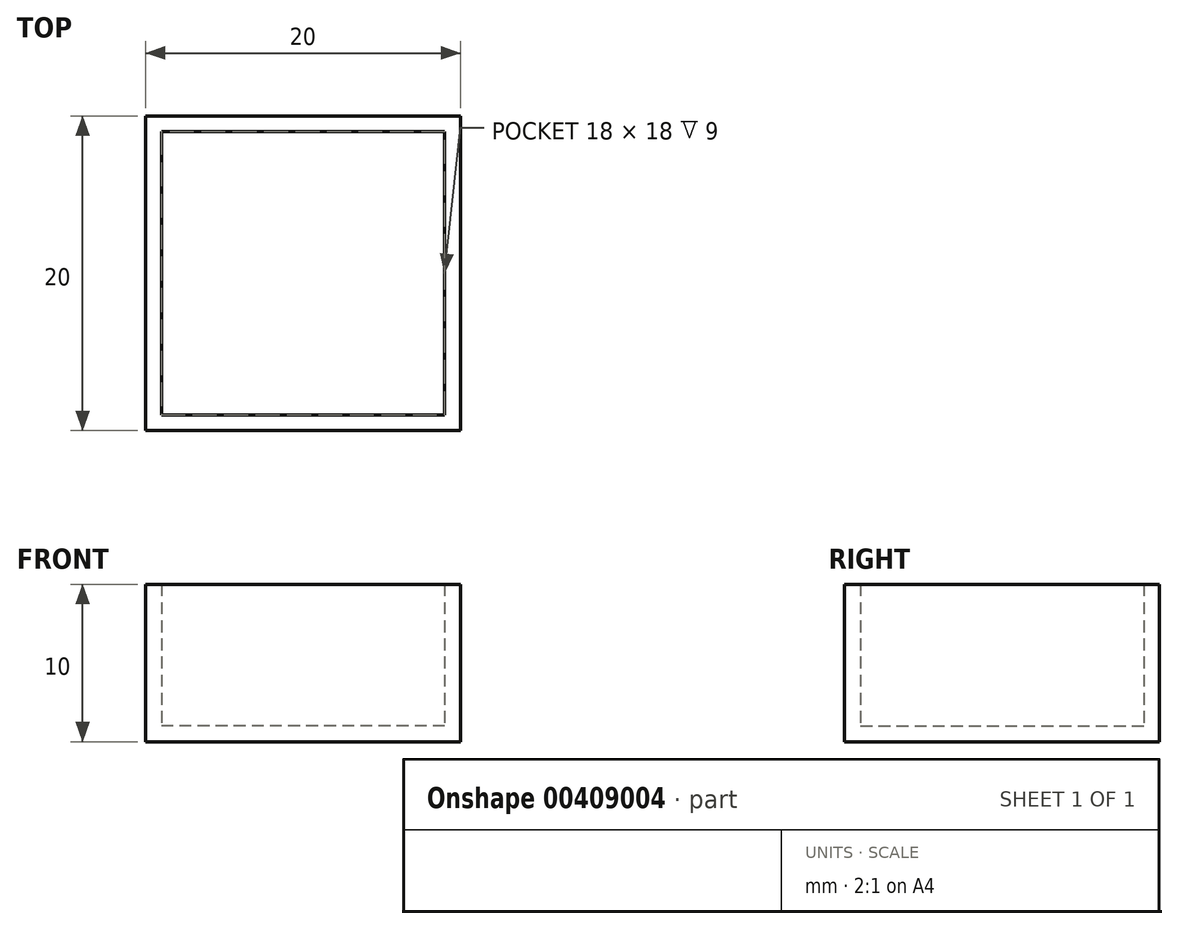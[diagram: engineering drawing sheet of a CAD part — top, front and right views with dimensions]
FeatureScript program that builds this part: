
annotation { "Feature Type Name" : "Feature", "Feature Type Description" : "" }
export const myFeature = defineFeature(function(context is Context, id is Id, definition is map)
    precondition{}
    {
        {
            var Q0;
            Q0=qCreatedBy(makeId("Top.planeOp"),FACE);
            var sketch = newSketch(context, id + "F0", { "sketchPlane" : qUnion([Q0])});
            skLineSegment(sketch, "E0.bottom", {"start": v(-10, 10) * mm, "end": v(10, 10) * mm});
            skLineSegment(sketch, "E0.top", {"start": v(-10, -10) * mm, "end": v(10, -10) * mm});
            skLineSegment(sketch, "E0.left", {"start": v(-10, 10) * mm, "end": v(-10, -10) * mm});
            skLineSegment(sketch, "E0.right", {"start": v(10, 10) * mm, "end": v(10, -10) * mm});
            skPoint(sketch, "E0.middle", {"position": v(0, 0) * mm});
            skLineSegment(sketch, "E1.0", {"start": v(-9, 9) * mm, "end": v(9, 9) * mm});
            skLineSegment(sketch, "E1.1", {"start": v(-9, 9) * mm, "end": v(-9, -9) * mm});
            skLineSegment(sketch, "E1.2", {"start": v(-9, -9) * mm, "end": v(9, -9) * mm});
            skLineSegment(sketch, "E1.3", {"start": v(9, 9) * mm, "end": v(9, -9) * mm});
            skSolve(sketch);
        }
        {
            var Q0;
            Q0=makeQuery(id+"F0.imprint","IMPRINT",FACE,{"disambiguationData":[TD([[makeQuery(id+"F0.imprint","IMPRINT",EDGE,{"derivedFrom":sQuery(id+"F0.wireOp",EDGE,"E1.0")}),-1.0]])]});
            var Q1;
            Q1=makeQuery(id+"F0.imprint","IMPRINT",FACE,{"disambiguationData":[TD([[makeQuery(id+"F0.imprint","IMPRINT",EDGE,{"derivedFrom":sQuery(id+"F0.wireOp",EDGE,"E0.bottom")}),-1.0]])]});
            extrude(context, id + "F1", {"entities" : qUnion([Q0, Q1]), "depth" : 1 * mm});
        }
        {
            var Q0;
            Q0=makeQuery(id+"F0.imprint","IMPRINT",FACE,{"disambiguationData":[TD([[makeQuery(id+"F0.imprint","IMPRINT",EDGE,{"derivedFrom":sQuery(id+"F0.wireOp",EDGE,"E0.bottom")}),-1.0]])]});
            extrude(context, id + "F2", {"entities" : qUnion([Q0]), "operationType" : NewBodyOperationType.ADD, "depth" : 10 * mm, "offsetDistance" : 25 * mm});
        }
    });
